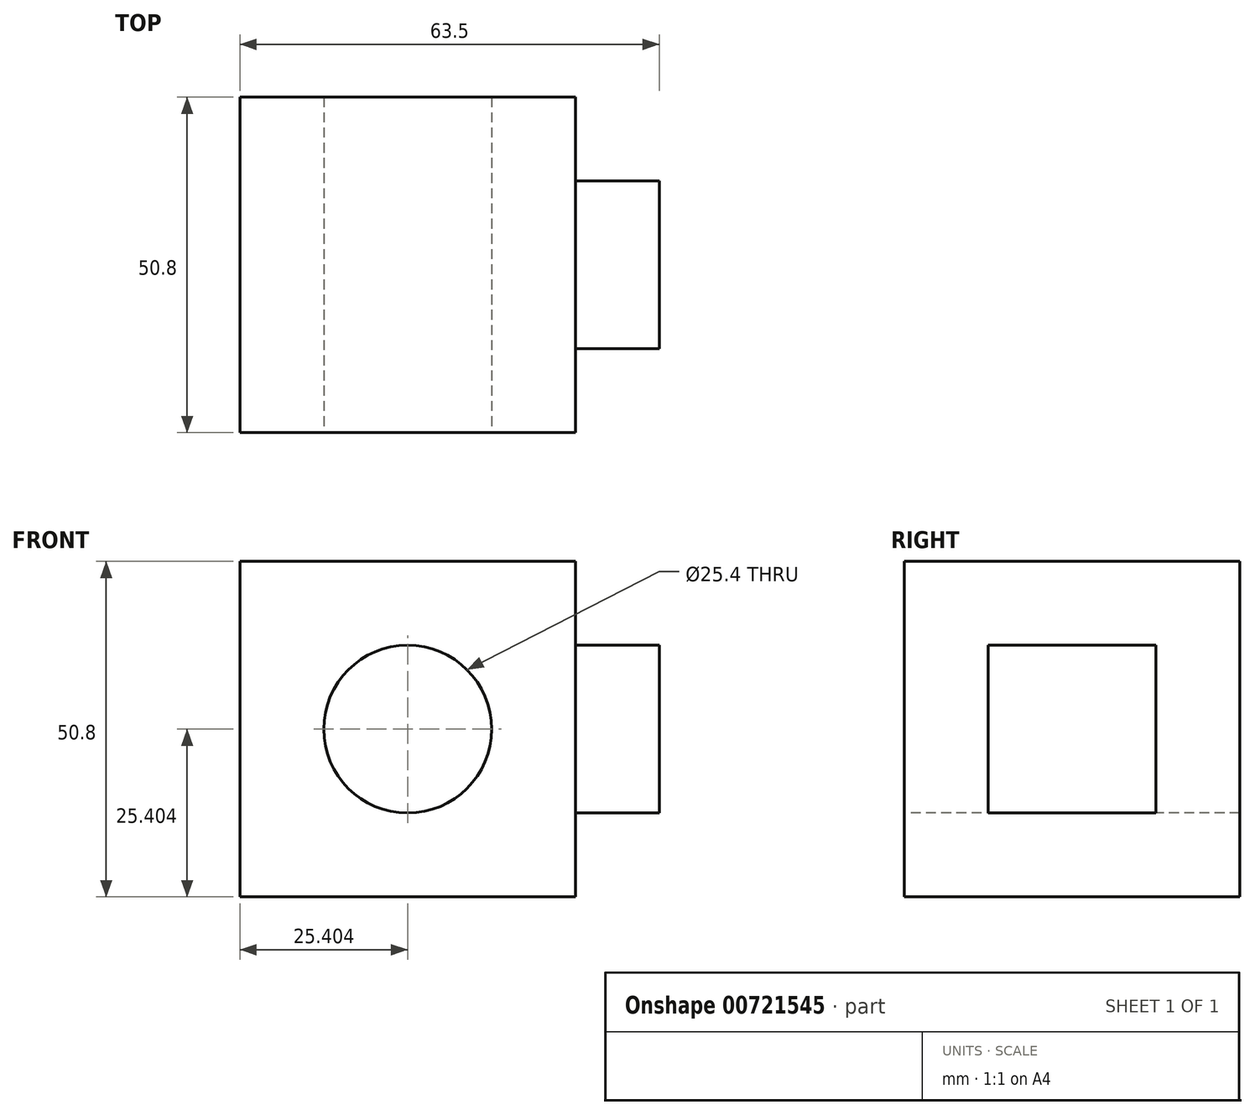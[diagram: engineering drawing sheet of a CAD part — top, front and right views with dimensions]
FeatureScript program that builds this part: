
annotation { "Feature Type Name" : "Feature", "Feature Type Description" : "" }
export const myFeature = defineFeature(function(context is Context, id is Id, definition is map)
    precondition{}
    {
        {
            var Q0;
            Q0=qCreatedBy(makeId("Front.planeOp"),FACE);
            var sketch = newSketch(context, id + "F0", { "sketchPlane" : qUnion([Q0])});
            skLineSegment(sketch, "E0.bottom", {"start": v(-31.08, 36.23) * mm, "end": v(19.72, 36.23) * mm});
            skLineSegment(sketch, "E0.top", {"start": v(-31.08, -14.57) * mm, "end": v(19.72, -14.57) * mm});
            skLineSegment(sketch, "E0.left", {"start": v(-31.08, 36.23) * mm, "end": v(-31.08, -14.57) * mm});
            skLineSegment(sketch, "E0.right", {"start": v(19.72, 36.23) * mm, "end": v(19.72, -14.57) * mm});
            skSolve(sketch);
        }
        {
            var Q0;
            Q0 = qSketchRegion(id + "F0", true);
            extrude(context, id + "F1", {"entities" : qUnion([Q0]), "depth" : 50.8 * mm, "offsetDistance" : 25.4 * mm});
        }
        {
            var Q0;
            Q0=makeQuery(id+"F1.opExtrude","CAP_FACE",FACE,{"disambiguationData":[OSD([sQuery(id+"F0.wireOp",EDGE,"E0.bottom"),sQuery(id+"F0.wireOp",EDGE,"E0.top"),sQuery(id+"F0.wireOp",EDGE,"E0.left"),sQuery(id+"F0.wireOp",EDGE,"E0.right")])],"isStart":false});
            var sketch = newSketch(context, id + "F2", { "sketchPlane" : qUnion([Q0])});
            skCircle(sketch, "E1", {"center": v(-5.68, 10.83) * mm, "radius": 12.7 * mm});
            skSolve(sketch);
        }
        {
            var Q0;
            Q0=makeQuery(id+"F2.imprint","IMPRINT",FACE,{"disambiguationData":[TD([[makeQuery(id+"F2.imprint","IMPRINT",EDGE,{"derivedFrom":sQuery(id+"F2.wireOp",EDGE,"E1")}),1.0]])]});
            extrude(context, id + "F3", {"entities" : qUnion([Q0]), "operationType" : NewBodyOperationType.REMOVE, "oppositeDirection" : true, "depth" : 50.8 * mm, "offsetDistance" : 25.4 * mm});
        }
        {
            var Q0;
            Q0=makeQuery(id+"F1.opExtrude","SWEPT_FACE",FACE,{"disambiguationData":[OSD([sQuery(id+"F0.wireOp",EDGE,"E0.right")])]});
            var sketch = newSketch(context, id + "F4", { "sketchPlane" : qUnion([Q0])});
            skLineSegment(sketch, "E2.bottom", {"start": v(-38.1, 23.53) * mm, "end": v(-12.7, 23.53) * mm});
            skLineSegment(sketch, "E2.top", {"start": v(-38.1, -1.87) * mm, "end": v(-12.7, -1.87) * mm});
            skLineSegment(sketch, "E2.left", {"start": v(-38.1, 23.53) * mm, "end": v(-38.1, -1.87) * mm});
            skLineSegment(sketch, "E2.right", {"start": v(-12.7, 23.53) * mm, "end": v(-12.7, -1.87) * mm});
            skSolve(sketch);
        }
        {
            var Q0;
            Q0 = qSketchRegion(id + "F4", true);
            extrude(context, id + "F5", {"entities" : qUnion([Q0]), "operationType" : NewBodyOperationType.ADD, "depth" : 12.7 * mm, "offsetDistance" : 25.4 * mm});
        }
    });
